# Revit family: EKF_EE_Рым-болтМ12Trivia_AVERES
name_source: partatom
category: Электрооборудование
units: mm (PartAtom-declared; Revit-internal decimal feet)

## family parameters
Всегда вертикально = Нет
На основе рабочей плоскости = Да
Общий = Да
При загрузке вырезать с полостями = Нет
Размер круглого соединителя = Использовать диаметр
Тип детали = Силовой щит
Точка расчета площади = Нет

## types (1)
- Рым-болты (4шт) М12 EKF AVERES
    ADSK_Единица измерения = шт.
    ADSK_Завод-изготовитель = EKF
    ADSK_Код изделия = ALR4M12
    ADSK_Количество = 1
    ADSK_Марка = Рым-болты (4 шт) М12 EKF AVERES
    ADSK_Масса = 0
    ADSK_Наименование = Рым-болты (4 шт) М12 EKF AVERES
    ADSK_Обозначение = Рым-болты (4 шт) М12 EKF AVERES
    ADSK_Размер_Высота = 73 мм
    ADSK_Размер_Глубина = 30 мм
    ADSK_Размер_Ширина = 54 мм
    Изготовитель = EKF
    Отметка по умолчанию = 1219.2 мм
    Серия номенклатуры = Averes
    Степень защиты IP = -
    ТВ = EKF_2_TRIVIA_AVERES
    Тип = 676 мм
    Тип установки = -
